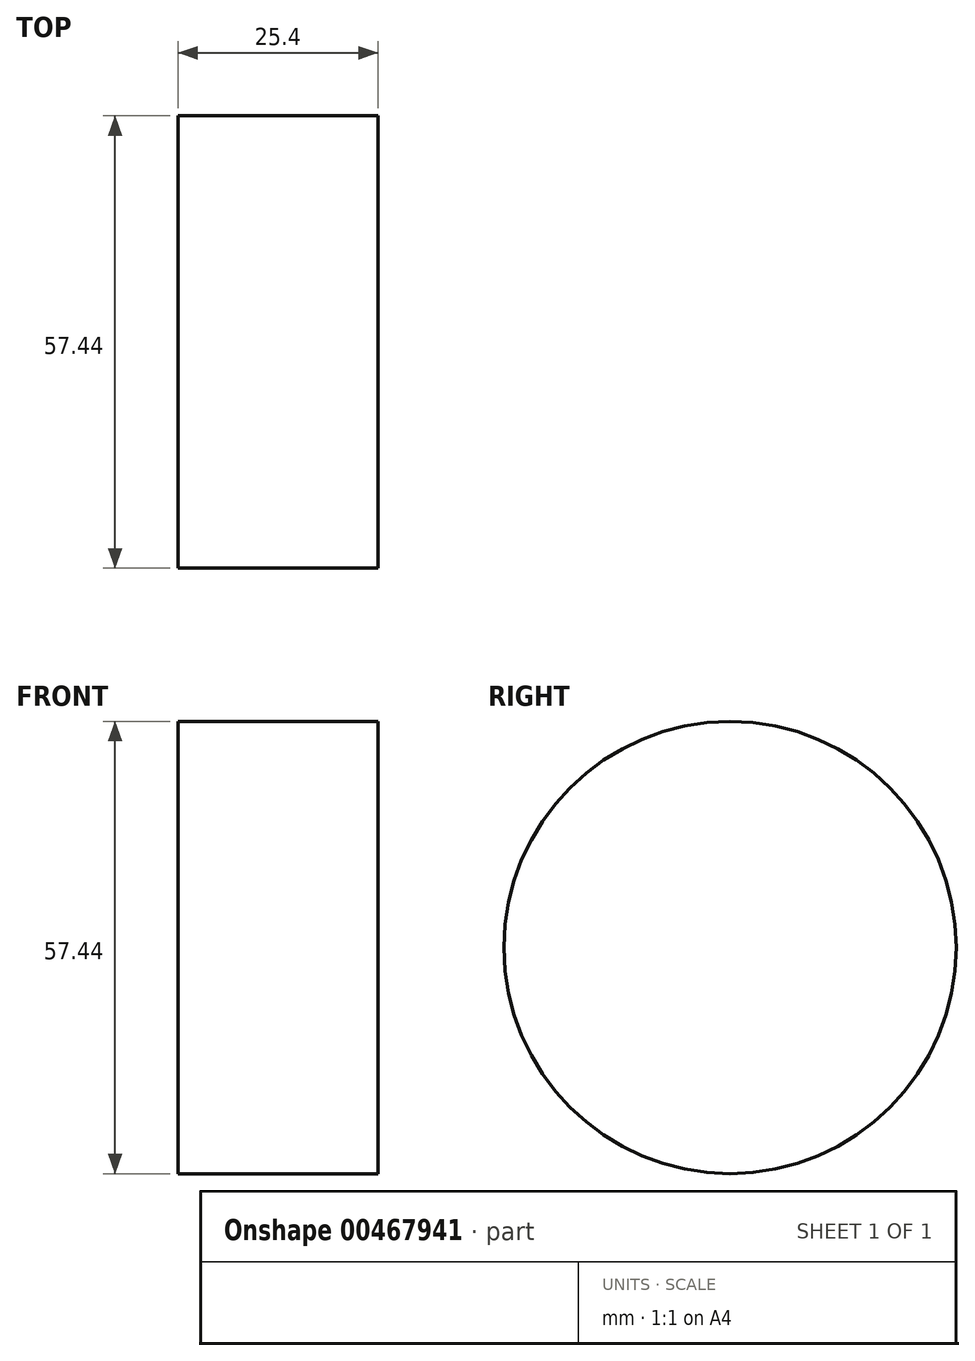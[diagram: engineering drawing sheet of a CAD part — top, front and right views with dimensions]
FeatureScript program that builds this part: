
annotation { "Feature Type Name" : "Feature", "Feature Type Description" : "" }
export const myFeature = defineFeature(function(context is Context, id is Id, definition is map)
    precondition{}
    {
        {
            var Q0;
            Q0=qCreatedBy(makeId("Right.planeOp"),FACE);
            var sketch = newSketch(context, id + "F0", { "sketchPlane" : qUnion([Q0])});
            skCircle(sketch, "E0", {"center": v(-50.08, 33.57) * mm, "radius": 28.72 * mm});
            skSolve(sketch);
        }
        {
            var Q0;
            Q0 = qSketchRegion(id + "F0", true);
            extrude(context, id + "F1", {"entities" : qUnion([Q0]), "depth" : 25.4 * mm});
        }
    });
